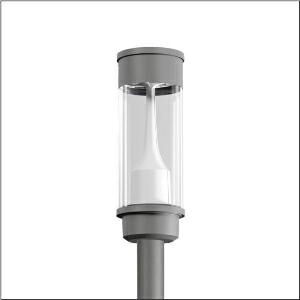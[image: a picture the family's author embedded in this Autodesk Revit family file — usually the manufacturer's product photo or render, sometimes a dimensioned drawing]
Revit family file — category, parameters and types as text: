
# Revit family: litepole_iq___p1_0a_5xa5415lf14h_d8b4
name_source: partatom
category: Lighting Fixtures
units: mm (PartAtom-declared; Revit-internal decimal feet)

## family parameters
Cut with Voids When Loaded = No
Host = Face
Light Source = No
Part Type = Normal
Room Calculation Point = No
Round Connector Dimension = Use Diameter
Shared = No

## types (1)
- --- (1 x LED, 1510 lm, 10 W, 4000K)
    Apparent Load = 10 VA
    CIE Flux Codes = 32 61 90 93 100
    Color Rendering = 70
    Color Temperature = 4000K
    Default Elevation = 1800 mm
    Description = Litepole iQ, mast luminaire, Module 540 iQ-SR, primary light control with 3 zone facetted reflector, of plastic, silver coated, highly specular, structured, primary optical cover: cover, of PMMA, transparent, partly coated, light distribution: P1.0a, light emission: direct distribution, primary light characteristic: strongly asymmetric, installation type: post-top, LED, High Power LED, rated luminous flux: 1.510lm, luminous efficacy: 151lm/W, light colour: 740, colour temperature: 4000K, control gear: ECG iQ, control: optimised constant luminous flux control (CLO 2.0), Desk-Remote (wireless, voltage-free reading and setting of iQ features in the workshop via application-optimized NFC function/RFID function), Light-Fading, Smart-Wire, Night-Set, Lumen-Switch, Temp-Guard, Auto-Match, Street-Remote, presetting dimming logarithmic, with terminal, 6-pole, max. 2.5mm², mains connection: 230..240V, AC, 50/60Hz, start of lifetime: 10W, end of service life: 10W, reduction: 5W, luminaire housing, upper part, of glass-fibre reinforced polyester, coated, Siteco® metallic grey (DB 702S), diameter: 210mm, height: 590mm, spigot size: d x l = 76 x 70mm (post-top) | with reducer (optional accessory) 60 x 70mm, post-top mast mounting element, of diecast aluminium, coated, Siteco® metallic grey (DB 702S), Module 540 iQ-SR, traffic white (RAL 9016), equipment: standard, protection rating (complete): IP65, insulation class (complete): insulation class II (safety insulation), certification: CE, ENEC, VDE, packaging unit: 1 piece

Light Distribution: P1.0a
    Height = 590 mm
    Lamp = 1 x LED
    Lamp Light Flux = 1510 lm
    Lamp Power = 10 W
    Lamp count = 1
    Length = 220 mm
    Luminous efficacy = 151 lm/W
    Manufacturer = Siteco
    ModVariant = No
    Model = 5XA5415LF14H
    Number of Poles = 1
    OnlyDefault = Yes
    Power Factor = 1
    Product Name = Litepole iQ | P1.0a
    Product group = mast luminaire | pylon top
    ProductGroupID = 6100
    Protection Class = Protection class II
    Protection Degree = IP 65
    RLX_Detail_Level = 1
    RLX_Emergency_Light_Flux = 0 lm
    RLX_Emergency_Type = 0
    RLX_Emergency_Type_DB = No
    RlxData = <blob elided: 68233 chars, md5=74c9c97c>
    Socket = socket
    Standby Power = 0 W
    System Light Flux = 1510 lm
    System Power = 10 W
    Type Comments = factory setting: luminous flux: 100 % | dim-lin: 254 | 401 mA
    Type Image = l_1006025.jpg
    URL = http://relux.com
    VarID = @adj_108873
    Voltage = 0 V
    Weight = 0.00 kg
    Width = 0 mm  [stored 0 ft]

note: [stored X ft] marks values corroborated as IEEE doubles in the binary element streams (Revit-internal decimal feet)

## geometry (parser evidence)
native form markers: Blend x4, Sweep x13
no freeform markers — native parametric forms only
